# Revit family: Zumtobel LINCOR A
name_source: partatom
category: Leuchten
revit_build: Autodesk Revit 2016 (Build: 20150714_1515(x64)
units: mm (PartAtom-declared; Revit-internal decimal feet)

## family parameters
Basisbauteil = Fläche
Beim Laden mit Abzugskörper schneiden = Nein
Bemaßung runder Anschluss = Durchmesser verwenden
Gemeinsam genutzt = Nein
Lichtquelle = Ja
OmniClass-Nummer = 23.80.70.11
OmniClass-Titel = Luminaries for Internal Lighting
Raumberechnungspunkt = Nein
Teiletyp = Normal

## types (1)
- LINCOR A D LED4200 L12 SR
    Baugruppenkennzeichen = D5020200
    Beschreibung = Pendant LED luminaire - darklight optic
    Cell 1209 = Ja
    Cell 2407 = Nein
    Datei für fotometrisches Netz = 42184429_(STD_LEO).IES
    Emissionsform beim Rendern sichtbar = Ja
    Farbfilter = 16777215
    Farbtemperaturverschiebung bei Dämpfen der Lampe = <Keine Auswahl>
    Height = 65 mm  [stored 0.213255 ft]
    Hersteller = Zumtobel Lighting
    Lampe = LED
    Length = 1209 mm  [stored 3.96654 ft]
    Modell = 42184429
    Neigungswinkel = 90.00°
    Scheinlast = 36 VA
    URL = http://www.zumtobel.com
    Voltage = 230 V
    Von Breite des Rechtecks ausssenden = 1199 mm  [stored 3.93373 ft]
    Von Länge des Rechtecks aussenden = 53 mm  [stored 0.173885 ft]
    Vorgabe-Ansicht = 0 mm  [stored 0 ft]
    Width = 63 mm  [stored 0.206693 ft]

note: [stored X ft] marks values corroborated as IEEE doubles in the binary element streams (Revit-internal decimal feet)

## geometry (parser evidence)
native form markers: Sweep x5
no freeform markers — native parametric forms only
